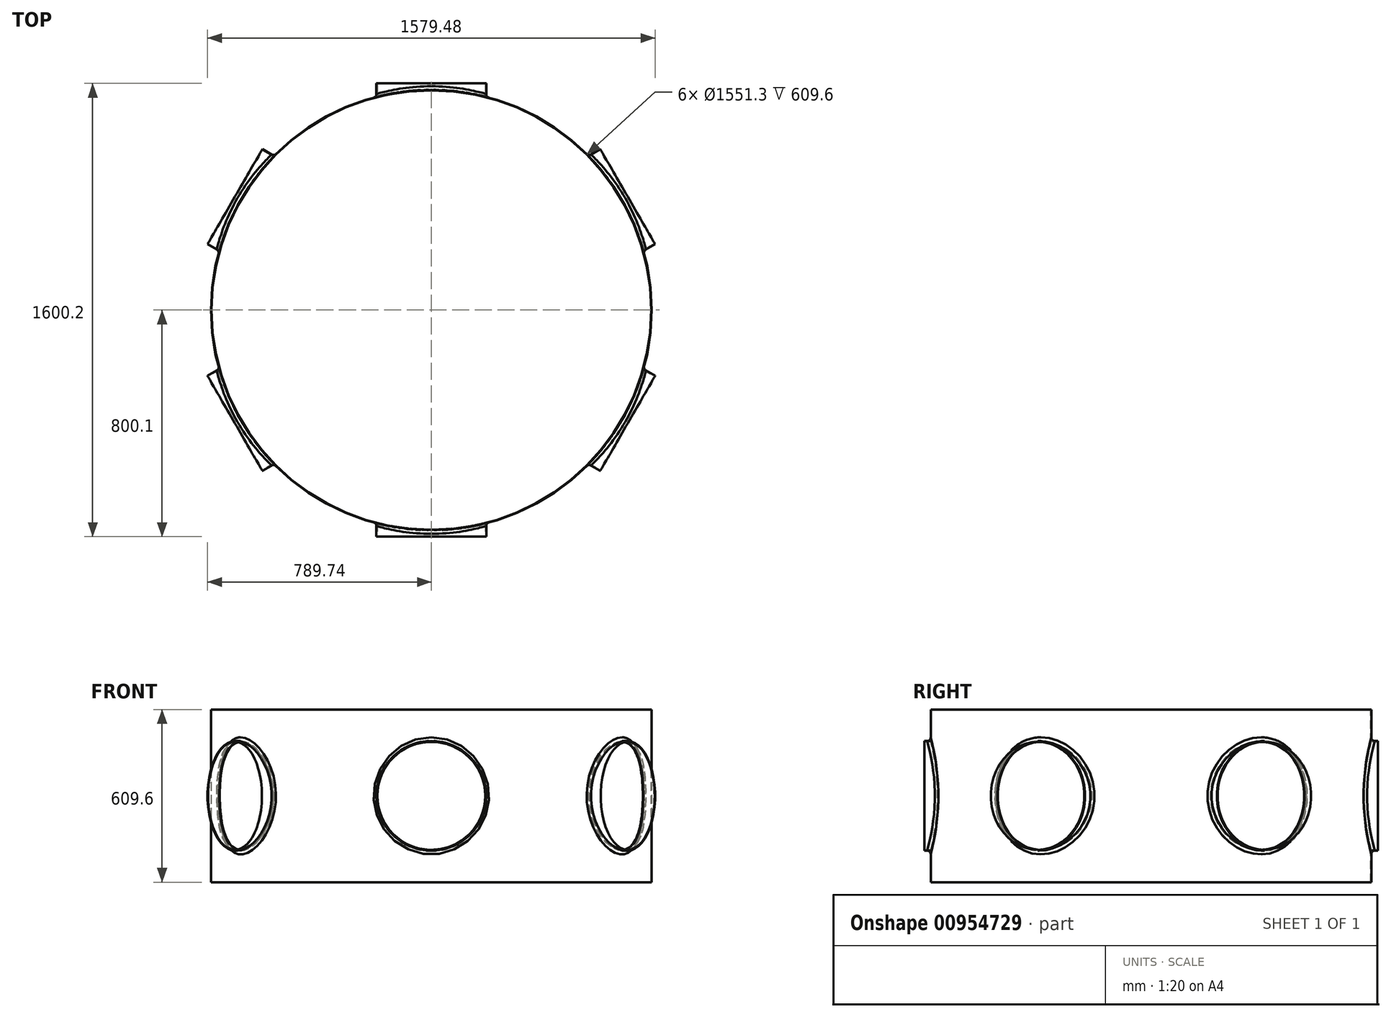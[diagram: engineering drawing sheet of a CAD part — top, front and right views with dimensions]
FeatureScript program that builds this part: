
annotation { "Feature Type Name" : "Feature", "Feature Type Description" : "" }
export const myFeature = defineFeature(function(context is Context, id is Id, definition is map)
    precondition{}
    {
        {
            var Q0;
            Q0=qCreatedBy(makeId("Top.planeOp"),FACE);
            var sketch = newSketch(context, id + "F0", { "sketchPlane" : qUnion([Q0])});
            skCircle(sketch, "E0", {"center": v(0, 0) * mm, "radius": 777.24 * mm});
            skSolve(sketch);
        }
        {
            var Q0;
            Q0=makeQuery(id+"F0.imprint","IMPRINT",FACE,{"disambiguationData":[TD([[makeQuery(id+"F0.imprint","IMPRINT",EDGE,{"derivedFrom":sQuery(id+"F0.wireOp",EDGE,"E0")}),1.0]])]});
            extrude(context, id + "F1", {"entities" : qUnion([Q0]), "depth" : 609.6 * mm, "offsetDistance" : 25.4 * mm});
        }
        {
            var Q0;
            Q0=qCreatedBy(makeId("Front.planeOp"),FACE);
            var sketch = newSketch(context, id + "F2", { "sketchPlane" : qUnion([Q0])});
            skLineSegment(sketch, "E1", {"start": v(0, 0) * mm, "end": v(0, 304.8) * mm});
            skCircle(sketch, "E2", {"center": v(0, 304.8) * mm, "radius": 193.68 * mm});
            skSolve(sketch);
        }
        {
            var Q0;
            Q0=makeQuery(id+"F2.imprint","IMPRINT",FACE,{"disambiguationData":[TD([[makeQuery(id+"F2.imprint","IMPRINT",EDGE,{"derivedFrom":sQuery(id+"F2.wireOp",EDGE,"E2")}),1.0]])]});
            extrude(context, id + "F3", {"entities" : qUnion([Q0]), "operationType" : NewBodyOperationType.ADD, "endBound" : BoundingType.SYMMETRIC, "depth" : 1600.2 * mm, "offsetDistance" : 25.4 * mm});
        }
        {
            var Q0;
            Q0=makeQuery(id+"F1.opExtrude","SWEPT_BODY",BODY,{"disambiguationData":[OSD([sQuery(id+"F0.wireOp",EDGE,"E0")])]});
            var Q1;
            Q1=makeQuery(id+"F1.opExtrude","CAP_EDGE",EDGE,{"disambiguationData":[OSD([sQuery(id+"F0.wireOp",EDGE,"E0")])],"isStart":false});
            circularPattern(context, id + "F4", {"entities" : qUnion([Q0]), "axis" : qUnion([Q1]), "angle" : 360 * degree, "instanceCount" : 6, "equalSpace" : true});
        }
        {
            var Q0;
            Q0=makeQuery(id+"F3.opExtrude","CAP_FACE",FACE,{"disambiguationData":[OSD([sQuery(id+"F2.wireOp",EDGE,"E2")])],"isStart":false});
            var sketch = newSketch(context, id + "F5", { "sketchPlane" : qUnion([Q0])});
            skCircle(sketch, "E3", {"center": v(0, 304.8) * mm, "radius": 190.5 * mm});
            skSolve(sketch);
        }
        {
            var Q0;
            Q0=makeQuery(id+"F5.imprint","IMPRINT",FACE,{"disambiguationData":[TD([[makeQuery(id+"F5.imprint","IMPRINT",EDGE,{"derivedFrom":sQuery(id+"F5.wireOp",EDGE,"E3")}),1.0]])]});
            extrude(context, id + "F6", {"entities" : qUnion([Q0]), "operationType" : NewBodyOperationType.REMOVE, "oppositeDirection" : true, "depth" : 1600.2 * mm, "offsetDistance" : 25.4 * mm});
        }
        {
            var Q0;
            Q0=makeQuery(id+"F1.opExtrude","CAP_FACE",FACE,{"disambiguationData":[OSD([sQuery(id+"F0.wireOp",EDGE,"E0")])],"isStart":false});
            var sketch = newSketch(context, id + "F7", { "sketchPlane" : qUnion([Q0])});
            skCircle(sketch, "E4", {"center": v(0, 0) * mm, "radius": 775.65 * mm});
            skSolve(sketch);
        }
        {
            var Q0;
            Q0=makeQuery(id+"F7.imprint","IMPRINT",FACE,{"disambiguationData":[TD([[makeQuery(id+"F7.imprint","IMPRINT",EDGE,{"derivedFrom":sQuery(id+"F7.wireOp",EDGE,"E4")}),1.0]])]});
            extrude(context, id + "F8", {"entities" : qUnion([Q0]), "operationType" : NewBodyOperationType.REMOVE, "oppositeDirection" : true, "depth" : 635 * mm, "offsetDistance" : 25.4 * mm});
        }
        {
            var Q0;
            Q0=makeQuery(id+"F4.opPattern","COPY",FACE,{"derivedFrom":makeQuery(id+"F3.opExtrude","CAP_FACE",FACE,{"disambiguationData":[OSD([sQuery(id+"F2.wireOp",EDGE,"E2")])],"isStart":true}),"instanceName":"2"});
            var sketch = newSketch(context, id + "F9", { "sketchPlane" : qUnion([Q0])});
            skCircle(sketch, "E5", {"center": v(0, 304.8) * mm, "radius": 190.5 * mm});
            skSolve(sketch);
        }
        {
            var Q0;
            Q0=makeQuery(id+"F9.imprint","IMPRINT",FACE,{"disambiguationData":[TD([[makeQuery(id+"F9.imprint","IMPRINT",EDGE,{"derivedFrom":sQuery(id+"F9.wireOp",EDGE,"E5")}),1.0]])]});
            extrude(context, id + "F10", {"entities" : qUnion([Q0]), "operationType" : NewBodyOperationType.REMOVE, "oppositeDirection" : true, "depth" : 1600.2 * mm, "offsetDistance" : 25.4 * mm});
        }
        {
            var Q0;
            Q0=makeQuery(id+"F4.opPattern","COPY",FACE,{"derivedFrom":makeQuery(id+"F3.opExtrude","CAP_FACE",FACE,{"disambiguationData":[OSD([sQuery(id+"F2.wireOp",EDGE,"E2")])],"isStart":false}),"instanceName":"1"});
            var sketch = newSketch(context, id + "F11", { "sketchPlane" : qUnion([Q0])});
            skCircle(sketch, "E6", {"center": v(0, 304.8) * mm, "radius": 190.5 * mm});
            skSolve(sketch);
        }
        {
            var Q0;
            Q0=makeQuery(id+"F11.imprint","IMPRINT",FACE,{"disambiguationData":[TD([[makeQuery(id+"F11.imprint","IMPRINT",EDGE,{"derivedFrom":sQuery(id+"F11.wireOp",EDGE,"E6")}),1.0]])]});
            extrude(context, id + "F12", {"entities" : qUnion([Q0]), "operationType" : NewBodyOperationType.REMOVE, "oppositeDirection" : true, "depth" : 1600.2 * mm, "offsetDistance" : 25.4 * mm});
        }
        {
            var Q0;
            Q0=makeQuery(id+"F4.opPattern","COPY",EDGE,{"derivedFrom":makeQuery(id+"F3.boolean.opBoolean","INTERSECT",EDGE,{"disambiguationData":[OD(0.0)],"derivedFrom":[makeQuery(id+"F1.opExtrude","SWEPT_FACE",FACE,{"disambiguationData":[OSD([sQuery(id+"F0.wireOp",EDGE,"E0")])]}),makeQuery(id+"F3.opExtrude","SWEPT_FACE",FACE,{"disambiguationData":[OSD([sQuery(id+"F2.wireOp",EDGE,"E2")])]})]}),"instanceName":"2"});
            var Q1;
            Q1=makeQuery(id+"F4.opPattern","COPY",EDGE,{"derivedFrom":makeQuery(id+"F3.boolean.opBoolean","INTERSECT",EDGE,{"disambiguationData":[OD(0.0)],"derivedFrom":[makeQuery(id+"F1.opExtrude","SWEPT_FACE",FACE,{"disambiguationData":[OSD([sQuery(id+"F0.wireOp",EDGE,"E0")])]}),makeQuery(id+"F3.opExtrude","SWEPT_FACE",FACE,{"disambiguationData":[OSD([sQuery(id+"F2.wireOp",EDGE,"E2")])]})]}),"instanceName":"1"});
            var Q2;
            Q2=makeQuery(id+"F3.boolean.opBoolean","INTERSECT",EDGE,{"disambiguationData":[OD(0.0)],"derivedFrom":[makeQuery(id+"F1.opExtrude","SWEPT_FACE",FACE,{"disambiguationData":[OSD([sQuery(id+"F0.wireOp",EDGE,"E0")])]}),makeQuery(id+"F3.opExtrude","SWEPT_FACE",FACE,{"disambiguationData":[OSD([sQuery(id+"F2.wireOp",EDGE,"E2")])]})]});
            var Q3;
            Q3=makeQuery(id+"F4.opPattern","COPY",EDGE,{"derivedFrom":makeQuery(id+"F3.boolean.opBoolean","INTERSECT",EDGE,{"disambiguationData":[OD(1.0)],"derivedFrom":[makeQuery(id+"F1.opExtrude","SWEPT_FACE",FACE,{"disambiguationData":[OSD([sQuery(id+"F0.wireOp",EDGE,"E0")])]}),makeQuery(id+"F3.opExtrude","SWEPT_FACE",FACE,{"disambiguationData":[OSD([sQuery(id+"F2.wireOp",EDGE,"E2")])]})]}),"instanceName":"2"});
            var Q4;
            Q4=makeQuery(id+"F4.opPattern","COPY",EDGE,{"derivedFrom":makeQuery(id+"F3.boolean.opBoolean","INTERSECT",EDGE,{"disambiguationData":[OD(1.0)],"derivedFrom":[makeQuery(id+"F1.opExtrude","SWEPT_FACE",FACE,{"disambiguationData":[OSD([sQuery(id+"F0.wireOp",EDGE,"E0")])]}),makeQuery(id+"F3.opExtrude","SWEPT_FACE",FACE,{"disambiguationData":[OSD([sQuery(id+"F2.wireOp",EDGE,"E2")])]})]}),"instanceName":"1"});
            var Q5;
            Q5=makeQuery(id+"F3.boolean.opBoolean","INTERSECT",EDGE,{"disambiguationData":[OD(1.0)],"derivedFrom":[makeQuery(id+"F1.opExtrude","SWEPT_FACE",FACE,{"disambiguationData":[OSD([sQuery(id+"F0.wireOp",EDGE,"E0")])]}),makeQuery(id+"F3.opExtrude","SWEPT_FACE",FACE,{"disambiguationData":[OSD([sQuery(id+"F2.wireOp",EDGE,"E2")])]})]});
            fillet(context, id + "F13", {"entities" : qUnion([Q0, Q1, Q2, Q3, Q4, Q5]), "radius" : 12.7 * mm, "tangentPropagation" : true, "allowEdgeOverflow" : false});
        }
    });
